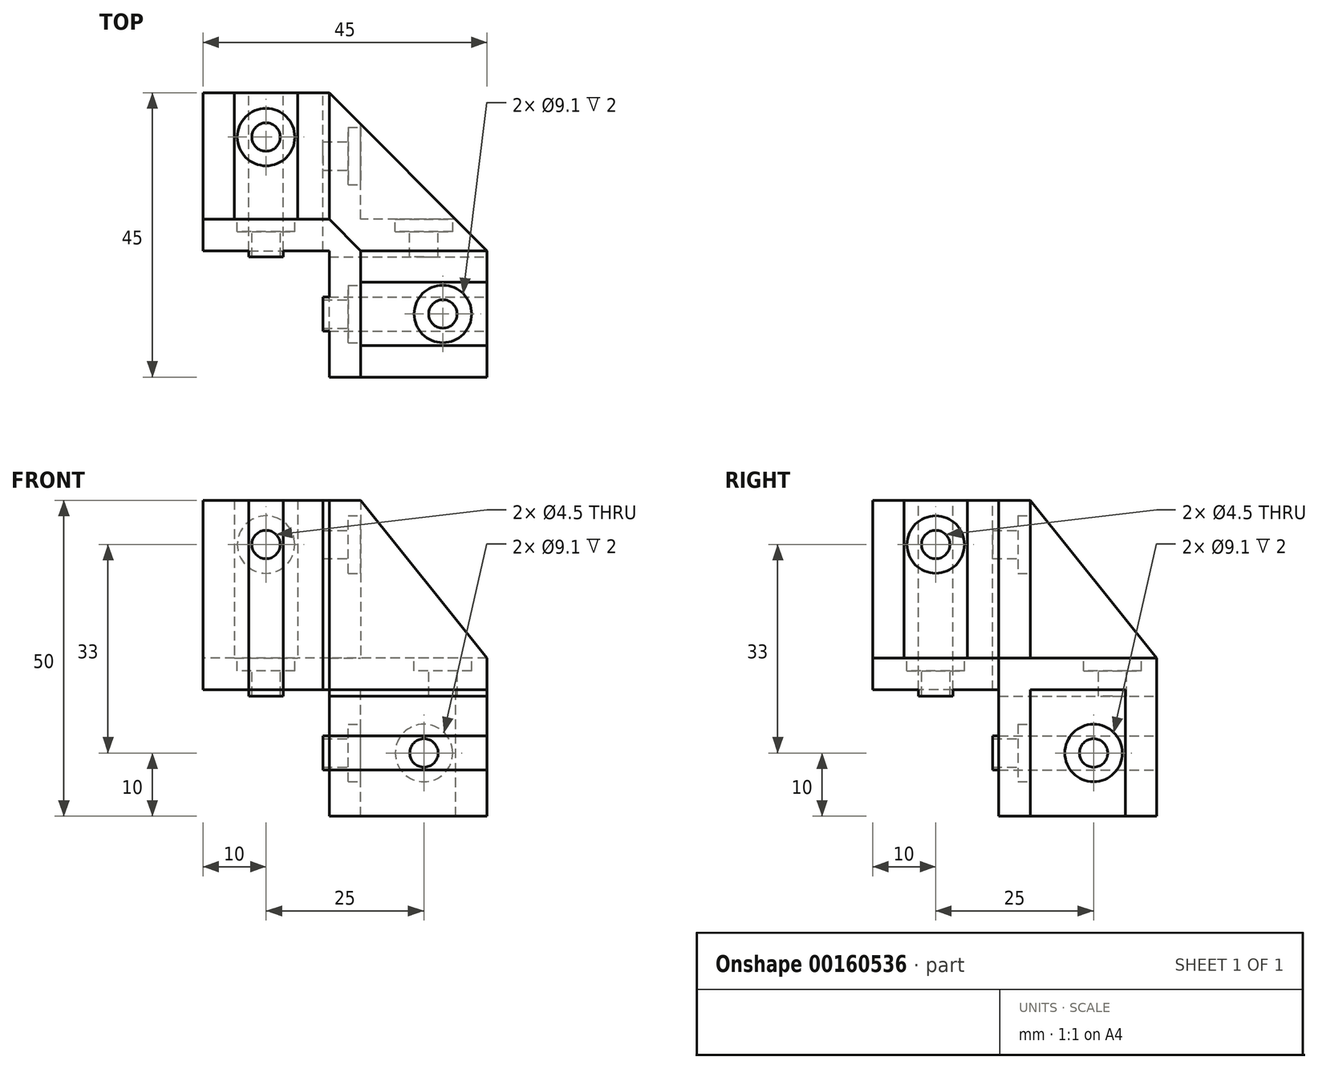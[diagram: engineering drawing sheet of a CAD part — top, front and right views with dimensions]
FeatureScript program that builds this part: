
annotation { "Feature Type Name" : "Feature", "Feature Type Description" : "" }
export const myFeature = defineFeature(function(context is Context, id is Id, definition is map)
    precondition{}
    {
        {
            var Q0;
            Q0=qCreatedBy(makeId("Top.planeOp"),FACE);
            var sketch = newSketch(context, id + "F0", { "sketchPlane" : qUnion([Q0])});
            skLineSegment(sketch, "E0", {"start": v(0, 0) * mm, "end": v(0, 60) * mm, "construction": true});
            skLineSegment(sketch, "E1", {"start": v(0, 60) * mm, "end": v(20, 60) * mm, "construction": true});
            skLineSegment(sketch, "E2", {"start": v(20, 60) * mm, "end": v(20, 20) * mm, "construction": true});
            skLineSegment(sketch, "E3", {"start": v(20, 20) * mm, "end": v(60, 20) * mm, "construction": true});
            skLineSegment(sketch, "E4", {"start": v(60, 20) * mm, "end": v(60, 0) * mm, "construction": true});
            skLineSegment(sketch, "E5", {"start": v(60, 0) * mm, "end": v(0, 0) * mm, "construction": true});
            skLineSegment(sketch, "E6", {"start": v(20, 20) * mm, "end": v(0, 20) * mm});
            skLineSegment(sketch, "E7", {"start": v(0, 20) * mm, "end": v(0, 45) * mm});
            skLineSegment(sketch, "E8", {"start": v(0, 45) * mm, "end": v(20, 45) * mm});
            skLineSegment(sketch, "E9", {"start": v(20, 20) * mm, "end": v(20, 0) * mm});
            skLineSegment(sketch, "E10", {"start": v(20, 0) * mm, "end": v(45, 0) * mm});
            skLineSegment(sketch, "E11", {"start": v(45, 0) * mm, "end": v(45, 20) * mm});
            skPoint(sketch, "E11.endSnap0", {"position": v(40, 20) * mm});
            skLineSegment(sketch, "E12", {"start": v(45, 20) * mm, "end": v(20, 45) * mm});
            skSolve(sketch);
        }
        {
            var Q0;
            Q0=makeQuery(id+"F0.imprint","IMPRINT",FACE,{"disambiguationData":[TD([[makeQuery(id+"F0.imprint","IMPRINT",EDGE,{"derivedFrom":sQuery(id+"F0.wireOp",EDGE,"E6")}),-1.0]])]});
            extrude(context, id + "F1", {"entities" : qUnion([Q0]), "depth" : 5 * mm});
        }
        {
            var Q0;
            Q0=makeQuery(id+"F1.opExtrude","CAP_FACE",FACE,{"disambiguationData":[OSD([sQuery(id+"F0.wireOp",EDGE,"E6"),sQuery(id+"F0.wireOp",EDGE,"E7"),sQuery(id+"F0.wireOp",EDGE,"E8"),sQuery(id+"F0.wireOp",EDGE,"E9"),sQuery(id+"F0.wireOp",EDGE,"E10"),sQuery(id+"F0.wireOp",EDGE,"E11"),sQuery(id+"F0.wireOp",EDGE,"E12")])],"isStart":false});
            var sketch = newSketch(context, id + "F2", { "sketchPlane" : qUnion([Q0])});
            skLineSegment(sketch, "E13", {"start": v(0, 20) * mm, "end": v(0, 25) * mm});
            skLineSegment(sketch, "E14", {"start": v(5, 25) * mm, "end": v(15, 25) * mm});
            skLineSegment(sketch, "E15", {"start": v(25, 15) * mm, "end": v(25, 5) * mm});
            skLineSegment(sketch, "E16", {"start": v(25, 0) * mm, "end": v(20, 0) * mm});
            skLineSegment(sketch, "E17", {"start": v(20, 0) * mm, "end": v(20, 20) * mm});
            skLineSegment(sketch, "E18", {"start": v(20, 20) * mm, "end": v(0, 20) * mm});
            skLineSegment(sketch, "E19", {"start": v(20, 45) * mm, "end": v(20, 25) * mm});
            skLineSegment(sketch, "E20", {"start": v(20, 45) * mm, "end": v(15, 45) * mm});
            skLineSegment(sketch, "E21", {"start": v(15, 45) * mm, "end": v(15, 25) * mm});
            skLineSegment(sketch, "E22", {"start": v(0, 25) * mm, "end": v(0, 45) * mm});
            skLineSegment(sketch, "E23", {"start": v(0, 45) * mm, "end": v(5, 45) * mm});
            skLineSegment(sketch, "E24", {"start": v(5, 45) * mm, "end": v(5, 25) * mm});
            skLineSegment(sketch, "E25", {"start": v(45, 20) * mm, "end": v(25, 20) * mm});
            skLineSegment(sketch, "E26", {"start": v(45, 20) * mm, "end": v(45, 15) * mm});
            skLineSegment(sketch, "E27", {"start": v(45, 15) * mm, "end": v(25, 15) * mm});
            skLineSegment(sketch, "E28", {"start": v(45, 0) * mm, "end": v(45, 5) * mm});
            skLineSegment(sketch, "E29", {"start": v(45, 5) * mm, "end": v(25, 5) * mm});
            skLineSegment(sketch, "E30", {"start": v(45, 0) * mm, "end": v(25, 0) * mm});
            skLineSegment(sketch, "E31", {"start": v(20, 25) * mm, "end": v(25, 20) * mm});
            skSolve(sketch);
        }
        {
            var Q0;
            Q0 = qSketchRegion(id + "F2", true);
            extrude(context, id + "F3", {"entities" : qUnion([Q0]), "operationType" : NewBodyOperationType.ADD, "depth" : 25 * mm});
        }
        {
            var Q0;
            Q0 = qSketchRegion(id + "F2", true);
            extrude(context, id + "F4", {"entities" : qUnion([Q0]), "operationType" : NewBodyOperationType.ADD, "depth" : 25 * mm});
        }
        {
            var Q0;
            Q0=makeQuery(id+"F3.boolean.opBoolean","MERGE",FACE,{"derivedFrom":[makeQuery(id+"F1.opExtrude","SWEPT_FACE",FACE,{"disambiguationData":[OSD([sQuery(id+"F0.wireOp",EDGE,"E7")])]}),makeQuery(id+"F3.opExtrude","SWEPT_FACE",FACE,{"disambiguationData":[OSD([sQuery(id+"F2.wireOp",EDGE,"E13"),sQuery(id+"F2.wireOp",EDGE,"E22")])]})]});
            var sketch = newSketch(context, id + "F5", { "sketchPlane" : qUnion([Q0])});
            skLineSegment(sketch, "E32", {"start": v(-20, 30) * mm, "end": v(-25, 30) * mm, "construction": true});
            skLineSegment(sketch, "E33", {"start": v(-45, 0) * mm, "end": v(-45, 5) * mm, "construction": true});
            skLineSegment(sketch, "E34", {"start": v(-45, 5) * mm, "end": v(-25, 30) * mm});
            skLineSegment(sketch, "E35", {"start": v(-25, 30) * mm, "end": v(-45, 30) * mm});
            skLineSegment(sketch, "E36", {"start": v(-45, 30) * mm, "end": v(-45, 5) * mm});
            skSolve(sketch);
        }
        {
            var Q0;
            Q0 = qSketchRegion(id + "F5", true);
            extrude(context, id + "F6", {"entities" : qUnion([Q0]), "operationType" : NewBodyOperationType.REMOVE, "endBound" : BoundingType.THROUGH_ALL, "oppositeDirection" : true, "depth" : 25 * mm});
        }
        {
            var Q0;
            {var subQ0=sQuery(id+"F0.wireOp",EDGE,"E6");var subQ1=sQuery(id+"F11.wireOp",EDGE,"E47");var subQ2=sQuery(id+"F11.wireOp",EDGE,"E46");var subQ3=sQuery(id+"F11.wireOp",EDGE,"E45");var subQ4=makeQuery(id+"F12.opExtrude","CAP_FACE",FACE,{"disambiguationData":[OSD([sQuery(id+"F11.wireOp",EDGE,"E44"),subQ3,subQ2,subQ1,sQuery(id+"F11.wireOp",EDGE,"E48")])],"isStart":false});var subQ5=sQuery(id+"F0.wireOp",EDGE,"E9");var subQ6=sQuery(id+"F0.wireOp",EDGE,"E12");var subQ7=sQuery(id+"F0.wireOp",EDGE,"E8");var subQ8=sQuery(id+"F0.wireOp",EDGE,"E7");var subQ9=makeQuery(id+"F1.opExtrude","CAP_FACE",FACE,{"disambiguationData":[OSD([subQ0,subQ8,subQ7,subQ5,sQuery(id+"F0.wireOp",EDGE,"E10"),sQuery(id+"F0.wireOp",EDGE,"E11"),subQ6])],"isStart":true});var subQ10=makeQuery(id+"F12.opExtrude","CAP_FACE",FACE,{"disambiguationData":[OSD([sQuery(id+"F11.wireOp",EDGE,"E49"),sQuery(id+"F11.wireOp",EDGE,"E50"),sQuery(id+"F11.wireOp",EDGE,"E51"),sQuery(id+"F11.wireOp",EDGE,"E52"),sQuery(id+"F11.wireOp",EDGE,"E53")])],"isStart":false});Q0=makeQuery(id+"F20.boolean.opBoolean","SPLIT",FACE,{"disambiguationData":[TD([makeQuery(id+"F1.opExtrude","SWEPT_FACE",FACE,{"disambiguationData":[OSD([subQ8])]})])],"derivedFrom":makeQuery(id+"F12.boolean.opBoolean","MERGE",FACE,{"derivedFrom":[subQ9,subQ4,subQ10]})});}
            var sketch = newSketch(context, id + "F7", { "sketchPlane" : qUnion([Q0])});
            skLineSegment(sketch, "E37.bottom", {"start": v(18, -7.29) * mm, "end": v(45, -7.29) * mm});
            skLineSegment(sketch, "E37.top", {"start": v(18, -12.7) * mm, "end": v(45, -12.7) * mm});
            skLineSegment(sketch, "E37.left", {"start": v(18, -7.29) * mm, "end": v(18, -12.7) * mm});
            skLineSegment(sketch, "E37.right", {"start": v(45, -7.29) * mm, "end": v(45, -12.7) * mm});
            skPoint(sketch, "E38.oppositeSnap0", {"position": v(12.71, -19) * mm});
            skLineSegment(sketch, "E38.bottom", {"start": v(7.3, -18) * mm, "end": v(12.71, -18) * mm});
            skLineSegment(sketch, "E38.top", {"start": v(7.3, -45) * mm, "end": v(12.71, -45) * mm});
            skLineSegment(sketch, "E38.left", {"start": v(7.3, -18) * mm, "end": v(7.3, -45) * mm});
            skLineSegment(sketch, "E38.right", {"start": v(12.71, -18) * mm, "end": v(12.71, -45) * mm});
            skSolve(sketch);
        }
        {
            var Q0;
            Q0 = qSketchRegion(id + "F7", true);
            extrude(context, id + "F8", {"entities" : qUnion([Q0]), "operationType" : NewBodyOperationType.ADD, "flatOperationType" : FlatOperationType.REMOVE, "offsetDistance" : 25 * mm, "depth" : 1 * mm, "domain" : OperationDomain.MODEL});
        }
        {
            var Q0;
            Q0=makeQuery(id+"F3.boolean.opBoolean","MERGE",FACE,{"derivedFrom":[makeQuery(id+"F1.opExtrude","SWEPT_FACE",FACE,{"disambiguationData":[OSD([sQuery(id+"F0.wireOp",EDGE,"E10")])]}),makeQuery(id+"F3.opExtrude","SWEPT_FACE",FACE,{"disambiguationData":[OSD([sQuery(id+"F2.wireOp",EDGE,"E16"),sQuery(id+"F2.wireOp",EDGE,"E30")])]})]});
            var sketch = newSketch(context, id + "F9", { "sketchPlane" : qUnion([Q0])});
            skLineSegment(sketch, "E39", {"start": v(20, 30) * mm, "end": v(25, 30) * mm, "construction": true});
            skLineSegment(sketch, "E40", {"start": v(25, 30) * mm, "end": v(45, 5) * mm});
            skLineSegment(sketch, "E41", {"start": v(45, 5) * mm, "end": v(45, 0) * mm, "construction": true});
            skLineSegment(sketch, "E42", {"start": v(25, 30) * mm, "end": v(45, 30) * mm});
            skLineSegment(sketch, "E43", {"start": v(45, 30) * mm, "end": v(45, 5) * mm});
            skSolve(sketch);
        }
        {
            var Q0;
            Q0 = qSketchRegion(id + "F9", true);
            extrude(context, id + "F10", {"entities" : qUnion([Q0]), "operationType" : NewBodyOperationType.REMOVE, "endBound" : BoundingType.THROUGH_ALL, "oppositeDirection" : true, "depth" : 25 * mm});
        }
        {
            var Q0;
            Q0=makeQuery(id+"F3.opExtrude","CAP_FACE",FACE,{"disambiguationData":[OSD([sQuery(id+"F2.wireOp",EDGE,"E13"),sQuery(id+"F2.wireOp",EDGE,"E14"),sQuery(id+"F2.wireOp",EDGE,"E15"),sQuery(id+"F2.wireOp",EDGE,"E16"),sQuery(id+"F2.wireOp",EDGE,"E17"),sQuery(id+"F2.wireOp",EDGE,"E18"),sQuery(id+"F2.wireOp",EDGE,"E19"),sQuery(id+"F2.wireOp",EDGE,"E20"),sQuery(id+"F2.wireOp",EDGE,"E21"),sQuery(id+"F2.wireOp",EDGE,"E22"),sQuery(id+"F2.wireOp",EDGE,"E23"),sQuery(id+"F2.wireOp",EDGE,"E24"),sQuery(id+"F2.wireOp",EDGE,"E25"),sQuery(id+"F2.wireOp",EDGE,"E26"),sQuery(id+"F2.wireOp",EDGE,"E27"),sQuery(id+"F2.wireOp",EDGE,"E28"),sQuery(id+"F2.wireOp",EDGE,"E29"),sQuery(id+"F2.wireOp",EDGE,"E30"),sQuery(id+"F2.wireOp",EDGE,"E31")])],"isStart":false});
            var sketch = newSketch(context, id + "F11", { "sketchPlane" : qUnion([Q0])});
            skLineSegment(sketch, "E44", {"start": v(10, 20) * mm, "end": v(12.71, 20) * mm});
            skLineSegment(sketch, "E45", {"start": v(12.71, 20) * mm, "end": v(12.71, 19) * mm});
            skLineSegment(sketch, "E46", {"start": v(12.71, 19) * mm, "end": v(7.3, 19) * mm});
            skLineSegment(sketch, "E47", {"start": v(7.3, 19) * mm, "end": v(7.3, 20) * mm});
            skLineSegment(sketch, "E48", {"start": v(7.3, 20) * mm, "end": v(10, 20) * mm});
            skLineSegment(sketch, "E49", {"start": v(20, 10) * mm, "end": v(20, 12.7) * mm});
            skLineSegment(sketch, "E50", {"start": v(20, 12.7) * mm, "end": v(19, 12.7) * mm});
            skLineSegment(sketch, "E51", {"start": v(19, 12.7) * mm, "end": v(19, 7.29) * mm});
            skLineSegment(sketch, "E52", {"start": v(19, 7.29) * mm, "end": v(20, 7.29) * mm});
            skLineSegment(sketch, "E53", {"start": v(20, 7.29) * mm, "end": v(20, 10) * mm});
            skSolve(sketch);
        }
        {
            var Q0;
            Q0 = qSketchRegion(id + "F11", true);
            extrude(context, id + "F12", {"entities" : qUnion([Q0]), "operationType" : NewBodyOperationType.ADD, "oppositeDirection" : true, "depth" : 30 * mm});
        }
        {
            var Q0;
            {var subQ0=sQuery(id+"F0.wireOp",EDGE,"E8");Q0=makeQuery(id+"F3.boolean.opBoolean","SPLIT",FACE,{"disambiguationData":[TD([makeQuery(id+"F3.opExtrude","SWEPT_FACE",FACE,{"disambiguationData":[OSD([sQuery(id+"F2.wireOp",EDGE,"E14")])]})])],"derivedFrom":makeQuery(id+"F1.opExtrude","CAP_FACE",FACE,{"disambiguationData":[OSD([sQuery(id+"F0.wireOp",EDGE,"E6"),sQuery(id+"F0.wireOp",EDGE,"E7"),subQ0,sQuery(id+"F0.wireOp",EDGE,"E9"),sQuery(id+"F0.wireOp",EDGE,"E10"),sQuery(id+"F0.wireOp",EDGE,"E11"),sQuery(id+"F0.wireOp",EDGE,"E12")])],"isStart":false})});}
            var sketch = newSketch(context, id + "F13", { "sketchPlane" : qUnion([Q0])});
            skCircle(sketch, "E54", {"center": v(10, 38) * mm, "radius": 2.25 * mm});
            skCircle(sketch, "E55", {"center": v(38, 10) * mm, "radius": 2.25 * mm});
            skSolve(sketch);
        }
        {
            var Q0;
            Q0=makeQuery(id+"F13.imprint","IMPRINT",FACE,{"disambiguationData":[TD([[makeQuery(id+"F13.imprint","IMPRINT",EDGE,{"derivedFrom":sQuery(id+"F13.wireOp",EDGE,"E54")}),1.0]])]});
            var Q1;
            Q1=makeQuery(id+"F13.imprint","IMPRINT",FACE,{"disambiguationData":[TD([[makeQuery(id+"F13.imprint","IMPRINT",EDGE,{"derivedFrom":sQuery(id+"F13.wireOp",EDGE,"E55")}),1.0]])]});
            extrude(context, id + "F14", {"entities" : qUnion([Q0, Q1]), "operationType" : NewBodyOperationType.REMOVE, "endBound" : BoundingType.THROUGH_ALL, "oppositeDirection" : true, "depth" : 25 * mm});
        }
        {
            var Q0;
            Q0=makeQuery(id+"F3.opExtrude","SWEPT_FACE",FACE,{"disambiguationData":[OSD([sQuery(id+"F2.wireOp",EDGE,"E14")])]});
            var sketch = newSketch(context, id + "F15", { "sketchPlane" : qUnion([Q0])});
            skCircle(sketch, "E56", {"center": v(-10, 23) * mm, "radius": 2.25 * mm});
            skSolve(sketch);
        }
        {
            var Q0;
            Q0 = qSketchRegion(id + "F15", true);
            extrude(context, id + "F16", {"entities" : qUnion([Q0]), "operationType" : NewBodyOperationType.REMOVE, "endBound" : BoundingType.THROUGH_ALL, "oppositeDirection" : true, "depth" : 25 * mm});
        }
        {
            var Q0;
            Q0=makeQuery(id+"F3.opExtrude","SWEPT_FACE",FACE,{"disambiguationData":[OSD([sQuery(id+"F2.wireOp",EDGE,"E15")])]});
            var sketch = newSketch(context, id + "F17", { "sketchPlane" : qUnion([Q0])});
            skCircle(sketch, "E57", {"center": v(10, 23) * mm, "radius": 2.25 * mm});
            skSolve(sketch);
        }
        {
            var Q0;
            Q0 = qSketchRegion(id + "F17", true);
            extrude(context, id + "F18", {"entities" : qUnion([Q0]), "operationType" : NewBodyOperationType.REMOVE, "endBound" : BoundingType.THROUGH_ALL, "oppositeDirection" : true, "depth" : 25 * mm});
        }
        {
            var Q0;
            Q0=makeQuery(id+"F1.opExtrude","CAP_FACE",FACE,{"disambiguationData":[OSD([sQuery(id+"F0.wireOp",EDGE,"E6"),sQuery(id+"F0.wireOp",EDGE,"E7"),sQuery(id+"F0.wireOp",EDGE,"E8"),sQuery(id+"F0.wireOp",EDGE,"E9"),sQuery(id+"F0.wireOp",EDGE,"E10"),sQuery(id+"F0.wireOp",EDGE,"E11"),sQuery(id+"F0.wireOp",EDGE,"E12")])],"isStart":true});
            var sketch = newSketch(context, id + "F19", { "sketchPlane" : qUnion([Q0])});
            skLineSegment(sketch, "E58", {"start": v(45, -20) * mm, "end": v(20, -20) * mm});
            skLineSegment(sketch, "E59", {"start": v(20, -20) * mm, "end": v(20, -45) * mm});
            skLineSegment(sketch, "E60", {"start": v(45, -20) * mm, "end": v(40, -25) * mm});
            skLineSegment(sketch, "E61", {"start": v(40, -25) * mm, "end": v(25, -25) * mm});
            skLineSegment(sketch, "E62", {"start": v(25, -25) * mm, "end": v(25, -40) * mm});
            skLineSegment(sketch, "E63", {"start": v(25, -40) * mm, "end": v(20, -45) * mm});
            skSolve(sketch);
        }
        {
            var Q0;
            Q0 = qSketchRegion(id + "F19", true);
            extrude(context, id + "F20", {"entities" : qUnion([Q0]), "operationType" : NewBodyOperationType.ADD, "depth" : 20 * mm});
        }
        {
            var Q0;
            Q0=makeQuery(id+"F20.opExtrude","SWEPT_FACE",FACE,{"disambiguationData":[OSD([sQuery(id+"F19.wireOp",EDGE,"E58")])]});
            var sketch = newSketch(context, id + "F21", { "sketchPlane" : qUnion([Q0])});
            skLineSegment(sketch, "E64", {"start": v(45, -10) * mm, "end": v(45, -12.71) * mm});
            skLineSegment(sketch, "E65", {"start": v(45, -12.71) * mm, "end": v(20, -12.71) * mm});
            skLineSegment(sketch, "E66", {"start": v(20, -12.71) * mm, "end": v(20, -7.3) * mm});
            skLineSegment(sketch, "E67", {"start": v(20, -7.3) * mm, "end": v(45, -7.3) * mm});
            skLineSegment(sketch, "E68", {"start": v(45, -7.3) * mm, "end": v(45, -10) * mm});
            skSolve(sketch);
        }
        {
            var Q0;
            Q0 = qSketchRegion(id + "F21", true);
            extrude(context, id + "F22", {"entities" : qUnion([Q0]), "operationType" : NewBodyOperationType.ADD, "flatOperationType" : FlatOperationType.REMOVE, "offsetDistance" : 25 * mm, "depth" : 1 * mm, "domain" : OperationDomain.MODEL});
        }
        {
            var Q0;
            Q0=makeQuery(id+"F22.boolean.opBoolean","MERGE",FACE,{"derivedFrom":[makeQuery(id+"F20.opExtrude","SWEPT_FACE",FACE,{"disambiguationData":[OSD([sQuery(id+"F19.wireOp",EDGE,"E59")])]}),makeQuery(id+"F22.opExtrude","SWEPT_FACE",FACE,{"disambiguationData":[OSD([sQuery(id+"F21.wireOp",EDGE,"E66")])]})]});
            var sketch = newSketch(context, id + "F23", { "sketchPlane" : qUnion([Q0])});
            skLineSegment(sketch, "E69.bottom", {"start": v(-19, -12.71) * mm, "end": v(-45, -12.71) * mm});
            skLineSegment(sketch, "E69.top", {"start": v(-19, -7.29) * mm, "end": v(-45, -7.3) * mm});
            skLineSegment(sketch, "E69.left", {"start": v(-19, -12.71) * mm, "end": v(-19, -7.3) * mm});
            skLineSegment(sketch, "E69.right", {"start": v(-45, -12.71) * mm, "end": v(-45, -7.3) * mm});
            skSolve(sketch);
        }
        {
            var Q0;
            Q0 = qSketchRegion(id + "F23", true);
            extrude(context, id + "F24", {"entities" : qUnion([Q0]), "operationType" : NewBodyOperationType.ADD, "flatOperationType" : FlatOperationType.REMOVE, "offsetDistance" : 25 * mm, "depth" : 1 * mm, "domain" : OperationDomain.MODEL});
        }
        {
            var Q0;
            Q0=makeQuery(id+"F20.opExtrude","SWEPT_FACE",FACE,{"disambiguationData":[OSD([sQuery(id+"F19.wireOp",EDGE,"E62")])]});
            var sketch = newSketch(context, id + "F25", { "sketchPlane" : qUnion([Q0])});
            skCircle(sketch, "E70", {"center": v(35, -10) * mm, "radius": 2.25 * mm});
            skPoint(sketch, "E70.centerSnap0", {"position": v(40, -10) * mm});
            skSolve(sketch);
        }
        {
            var Q0;
            Q0 = qSketchRegion(id + "F25", true);
            extrude(context, id + "F26", {"entities" : qUnion([Q0]), "operationType" : NewBodyOperationType.REMOVE, "endBound" : BoundingType.THROUGH_ALL, "oppositeDirection" : true, "depth" : 25 * mm});
        }
        {
            var Q0;
            Q0=makeQuery(id+"F20.opExtrude","SWEPT_FACE",FACE,{"disambiguationData":[OSD([sQuery(id+"F19.wireOp",EDGE,"E61")])]});
            var sketch = newSketch(context, id + "F27", { "sketchPlane" : qUnion([Q0])});
            skCircle(sketch, "E71", {"center": v(-35, -10) * mm, "radius": 2.25 * mm});
            skPoint(sketch, "E71.centerSnap0", {"position": v(-40, -10) * mm});
            skSolve(sketch);
        }
        {
            var Q0;
            Q0=makeQuery(id+"F27.imprint","IMPRINT",FACE,{"disambiguationData":[TD([[makeQuery(id+"F27.imprint","IMPRINT",EDGE,{"derivedFrom":sQuery(id+"F27.wireOp",EDGE,"E71")}),1.0]])]});
            extrude(context, id + "F28", {"entities" : qUnion([Q0]), "operationType" : NewBodyOperationType.REMOVE, "endBound" : BoundingType.THROUGH_ALL, "oppositeDirection" : true, "depth" : 25 * mm});
        }
        {
            var Q0;
            Q0=makeQuery(id+"F20.opExtrude","SWEPT_FACE",FACE,{"disambiguationData":[OSD([sQuery(id+"F19.wireOp",EDGE,"E61")])]});
            var sketch = newSketch(context, id + "F29", { "sketchPlane" : qUnion([Q0])});
            skCircle(sketch, "E72", {"center": v(-35, -10) * mm, "radius": 4.55 * mm});
            skSolve(sketch);
        }
        {
            var Q0;
            Q0 = qSketchRegion(id + "F29", true);
            extrude(context, id + "F30", {"entities" : qUnion([Q0]), "operationType" : NewBodyOperationType.REMOVE, "oppositeDirection" : true, "depth" : 2 * mm});
        }
        {
            var Q0;
            Q0=makeQuery(id+"F20.opExtrude","SWEPT_FACE",FACE,{"disambiguationData":[OSD([sQuery(id+"F19.wireOp",EDGE,"E62")])]});
            var sketch = newSketch(context, id + "F31", { "sketchPlane" : qUnion([Q0])});
            skCircle(sketch, "E73", {"center": v(35, -10) * mm, "radius": 4.55 * mm});
            skSolve(sketch);
        }
        {
            var Q0;
            Q0 = qSketchRegion(id + "F31", true);
            extrude(context, id + "F32", {"entities" : qUnion([Q0]), "operationType" : NewBodyOperationType.REMOVE, "oppositeDirection" : true, "depth" : 2 * mm});
        }
        {
            var Q0;
            Q0=makeQuery(id+"F3.opExtrude","SWEPT_FACE",FACE,{"disambiguationData":[OSD([sQuery(id+"F2.wireOp",EDGE,"E14")])]});
            var sketch = newSketch(context, id + "F33", { "sketchPlane" : qUnion([Q0])});
            skCircle(sketch, "E74", {"center": v(-10, 23) * mm, "radius": 4.55 * mm});
            skSolve(sketch);
        }
        {
            var Q0;
            Q0 = qSketchRegion(id + "F33", true);
            extrude(context, id + "F34", {"entities" : qUnion([Q0]), "operationType" : NewBodyOperationType.REMOVE, "oppositeDirection" : true, "depth" : 2 * mm});
        }
        {
            var Q0;
            Q0=makeQuery(id+"F3.opExtrude","SWEPT_FACE",FACE,{"disambiguationData":[OSD([sQuery(id+"F2.wireOp",EDGE,"E15")])]});
            var sketch = newSketch(context, id + "F35", { "sketchPlane" : qUnion([Q0])});
            skCircle(sketch, "E75", {"center": v(10, 23) * mm, "radius": 4.55 * mm});
            skSolve(sketch);
        }
        {
            var Q0;
            Q0 = qSketchRegion(id + "F35", true);
            extrude(context, id + "F36", {"entities" : qUnion([Q0]), "operationType" : NewBodyOperationType.REMOVE, "oppositeDirection" : true, "depth" : 2 * mm});
        }
        {
            var Q0;
            {var subQ0=sQuery(id+"F0.wireOp",EDGE,"E11");Q0=makeQuery(id+"F3.boolean.opBoolean","SPLIT",FACE,{"disambiguationData":[TD([makeQuery(id+"F3.opExtrude","SWEPT_FACE",FACE,{"disambiguationData":[OSD([sQuery(id+"F2.wireOp",EDGE,"E15")])]})])],"derivedFrom":makeQuery(id+"F1.opExtrude","CAP_FACE",FACE,{"disambiguationData":[OSD([sQuery(id+"F0.wireOp",EDGE,"E6"),sQuery(id+"F0.wireOp",EDGE,"E7"),sQuery(id+"F0.wireOp",EDGE,"E8"),sQuery(id+"F0.wireOp",EDGE,"E9"),sQuery(id+"F0.wireOp",EDGE,"E10"),subQ0,sQuery(id+"F0.wireOp",EDGE,"E12")])],"isStart":false})});}
            var sketch = newSketch(context, id + "F37", { "sketchPlane" : qUnion([Q0])});
            skCircle(sketch, "E76", {"center": v(38, 10) * mm, "radius": 4.55 * mm});
            skSolve(sketch);
        }
        {
            var Q0;
            Q0 = qSketchRegion(id + "F37", true);
            extrude(context, id + "F38", {"entities" : qUnion([Q0]), "operationType" : NewBodyOperationType.REMOVE, "oppositeDirection" : true, "depth" : 2 * mm});
        }
        {
            var Q0;
            {var subQ0=sQuery(id+"F0.wireOp",EDGE,"E8");Q0=makeQuery(id+"F3.boolean.opBoolean","SPLIT",FACE,{"disambiguationData":[TD([makeQuery(id+"F3.opExtrude","SWEPT_FACE",FACE,{"disambiguationData":[OSD([sQuery(id+"F2.wireOp",EDGE,"E14")])]})])],"derivedFrom":makeQuery(id+"F1.opExtrude","CAP_FACE",FACE,{"disambiguationData":[OSD([sQuery(id+"F0.wireOp",EDGE,"E6"),sQuery(id+"F0.wireOp",EDGE,"E7"),subQ0,sQuery(id+"F0.wireOp",EDGE,"E9"),sQuery(id+"F0.wireOp",EDGE,"E10"),sQuery(id+"F0.wireOp",EDGE,"E11"),sQuery(id+"F0.wireOp",EDGE,"E12")])],"isStart":false})});}
            var sketch = newSketch(context, id + "F39", { "sketchPlane" : qUnion([Q0])});
            skCircle(sketch, "E77", {"center": v(10, 38) * mm, "radius": 4.55 * mm});
            skSolve(sketch);
        }
        {
            var Q0;
            Q0 = qSketchRegion(id + "F39", true);
            extrude(context, id + "F40", {"entities" : qUnion([Q0]), "operationType" : NewBodyOperationType.REMOVE, "oppositeDirection" : true, "depth" : 2 * mm});
        }
        {
            var Q0;
            Q0=makeQuery(id+"F24.boolean.opBoolean","MERGE",FACE,{"derivedFrom":[makeQuery(id+"F22.opExtrude","SWEPT_FACE",FACE,{"disambiguationData":[OSD([sQuery(id+"F21.wireOp",EDGE,"E67")])]}),makeQuery(id+"F24.opExtrude","SWEPT_FACE",FACE,{"disambiguationData":[OSD([sQuery(id+"F23.wireOp",EDGE,"E69.top")])]})]});
            var sketch = newSketch(context, id + "F41", { "sketchPlane" : qUnion([Q0])});
            skLineSegment(sketch, "E78.bottom", {"start": v(20, 20) * mm, "end": v(19, 20) * mm});
            skLineSegment(sketch, "E78.top", {"start": v(20, 19) * mm, "end": v(19, 19) * mm});
            skLineSegment(sketch, "E78.left", {"start": v(20, 20) * mm, "end": v(20, 19) * mm});
            skLineSegment(sketch, "E78.right", {"start": v(19, 20) * mm, "end": v(19, 19) * mm});
            skSolve(sketch);
        }
        {
            var Q0;
            Q0 = qSketchRegion(id + "F41", true);
            extrude(context, id + "F42", {"entities" : qUnion([Q0]), "operationType" : NewBodyOperationType.REMOVE, "endBound" : BoundingType.THROUGH_ALL, "oppositeDirection" : true, "depth" : 25 * mm});
        }
        {
            var Q0;
            Q0=makeQuery(id+"F12.boolean.opBoolean","MERGE",FACE,{"derivedFrom":[makeQuery(id+"F8.opExtrude","SWEPT_FACE",FACE,{"disambiguationData":[OSD([sQuery(id+"F7.wireOp",EDGE,"E38.right")])]}),makeQuery(id+"F12.opExtrude","SWEPT_FACE",FACE,{"disambiguationData":[OSD([sQuery(id+"F11.wireOp",EDGE,"E45")])]})]});
            var sketch = newSketch(context, id + "F43", { "sketchPlane" : qUnion([Q0])});
            skLineSegment(sketch, "E79.bottom", {"start": v(20, 0) * mm, "end": v(18, 0) * mm});
            skLineSegment(sketch, "E79.top", {"start": v(20, -1) * mm, "end": v(18, -1) * mm});
            skLineSegment(sketch, "E79.left", {"start": v(20, 0) * mm, "end": v(20, -1) * mm});
            skLineSegment(sketch, "E79.right", {"start": v(18, 0) * mm, "end": v(18, -1) * mm});
            skSolve(sketch);
        }
        {
            var Q0;
            Q0 = qSketchRegion(id + "F43", true);
            extrude(context, id + "F44", {"entities" : qUnion([Q0]), "operationType" : NewBodyOperationType.REMOVE, "endBound" : BoundingType.THROUGH_ALL, "oppositeDirection" : true, "depth" : 25 * mm});
        }
        {
            var Q0;
            Q0=makeQuery(id+"F12.boolean.opBoolean","MERGE",FACE,{"derivedFrom":[makeQuery(id+"F8.opExtrude","SWEPT_FACE",FACE,{"disambiguationData":[OSD([sQuery(id+"F7.wireOp",EDGE,"E37.top")])]}),makeQuery(id+"F12.opExtrude","SWEPT_FACE",FACE,{"disambiguationData":[OSD([sQuery(id+"F11.wireOp",EDGE,"E50")])]})]});
            var sketch = newSketch(context, id + "F45", { "sketchPlane" : qUnion([Q0])});
            skLineSegment(sketch, "E80.bottom", {"start": v(-20, 0) * mm, "end": v(-18, 0) * mm});
            skLineSegment(sketch, "E80.top", {"start": v(-20, -1) * mm, "end": v(-18, -1) * mm});
            skLineSegment(sketch, "E80.left", {"start": v(-20, 0) * mm, "end": v(-20, -1) * mm});
            skLineSegment(sketch, "E80.right", {"start": v(-18, 0) * mm, "end": v(-18, -1) * mm});
            skSolve(sketch);
        }
        {
            var Q0;
            Q0 = qSketchRegion(id + "F45", true);
            extrude(context, id + "F46", {"entities" : qUnion([Q0]), "operationType" : NewBodyOperationType.REMOVE, "endBound" : BoundingType.THROUGH_ALL, "oppositeDirection" : true, "depth" : 25 * mm});
        }
    });
